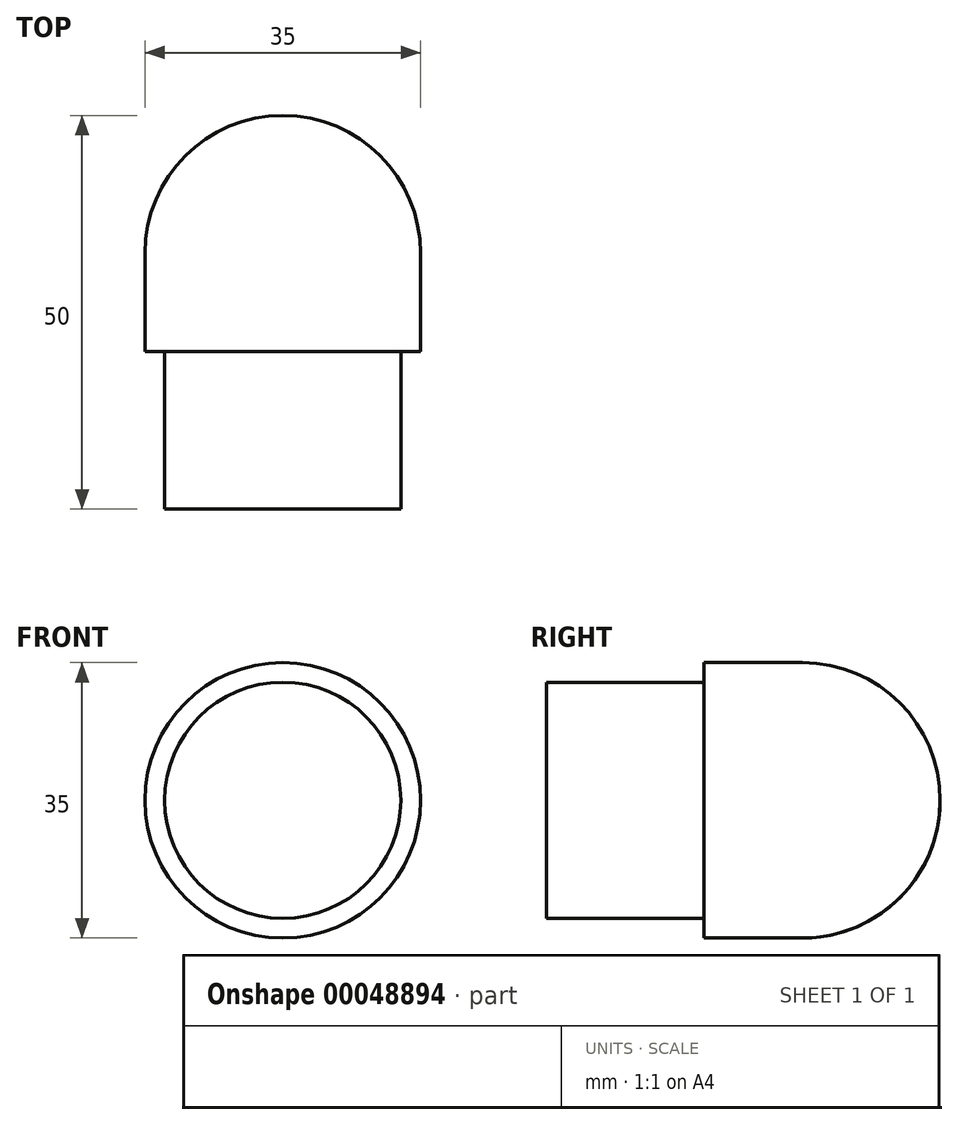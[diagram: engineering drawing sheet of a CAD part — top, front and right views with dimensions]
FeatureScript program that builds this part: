
annotation { "Feature Type Name" : "Feature", "Feature Type Description" : "" }
export const myFeature = defineFeature(function(context is Context, id is Id, definition is map)
    precondition{}
    {
        {
            var Q0;
            Q0=qCreatedBy(makeId("Right.planeOp"),FACE);
            var sketch = newSketch(context, id + "F0", { "sketchPlane" : qUnion([Q0])});
            skLineSegment(sketch, "E0.rect.bottom", {"start": v(25, 15) * mm, "end": v(-25, 15) * mm, "construction": true});
            skLineSegment(sketch, "E0.rect.top", {"start": v(25, -15) * mm, "end": v(-25, -15) * mm, "construction": true});
            skLineSegment(sketch, "E0.rect.left", {"start": v(25, 15) * mm, "end": v(25, -15) * mm, "construction": true});
            skLineSegment(sketch, "E0.rect.right", {"start": v(-25, 15) * mm, "end": v(-25, -15) * mm, "construction": true});
            skPoint(sketch, "E0.rect.middle", {"position": v(0, 0) * mm});
            skLineSegment(sketch, "E1", {"start": v(-25, 0) * mm, "end": v(-5, 0) * mm, "construction": true});
            skPoint(sketch, "E1.endSnap0", {"position": v(-25, 0) * mm});
            skLineSegment(sketch, "E2", {"start": v(-5, 0) * mm, "end": v(-5, 17.5) * mm, "construction": true});
            skLineSegment(sketch, "E3", {"start": v(-25, 0) * mm, "end": v(-25, 15) * mm});
            skLineSegment(sketch, "E4", {"start": v(-25, 15) * mm, "end": v(-5, 15) * mm});
            skLineSegment(sketch, "E5", {"start": v(-5, 15) * mm, "end": v(-5, 17.5) * mm});
            skLineSegment(sketch, "E6", {"start": v(-25, 0) * mm, "end": v(25, 0) * mm});
            skLineSegment(sketch, "E7", {"start": v(25, 0) * mm, "end": v(7.5, 0) * mm, "construction": true});
            skLineSegment(sketch, "E8", {"start": v(7.5, 0) * mm, "end": v(7.5, 17.5) * mm, "construction": true});
            skLineSegment(sketch, "E9", {"start": v(7.5, 17.5) * mm, "end": v(-5, 17.5) * mm});
            skArc(sketch, "E10", {"start": v(25, 0) * mm, "mid": v(19.87, 12.37) * mm, "end": v(7.5, 17.5) * mm});
            skSolve(sketch);
        }
        {
            var Q0;
            Q0=makeQuery(id+"F0.imprint","IMPRINT",FACE,{"disambiguationData":[TD([[makeQuery(id+"F0.imprint","IMPRINT",EDGE,{"derivedFrom":sQuery(id+"F0.wireOp",EDGE,"E3")}),-1.0]])]});
            var Q1;
            Q1=sQuery(id+"F0.wireOp",EDGE,"E6");
            revolve(context, id + "F1", {"entities" : qUnion([Q0]), "axis" : qUnion([Q1]), "revolveType" : RevolveType.FULL});
        }
    });
